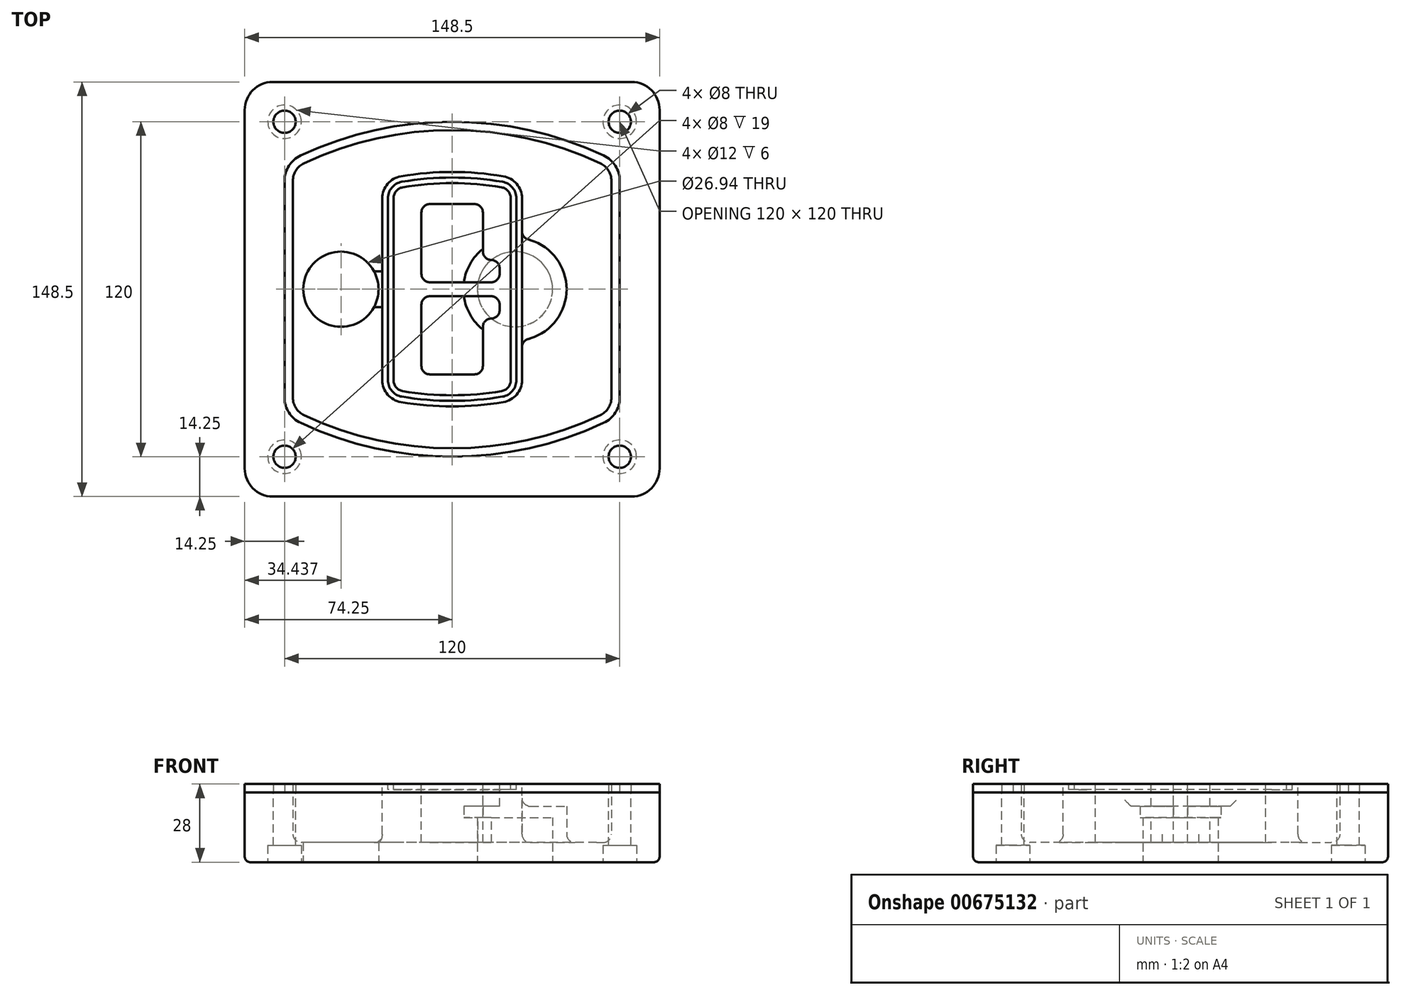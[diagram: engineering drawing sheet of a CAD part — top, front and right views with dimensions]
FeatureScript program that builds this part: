
annotation { "Feature Type Name" : "Feature", "Feature Type Description" : "" }
export const myFeature = defineFeature(function(context is Context, id is Id, definition is map)
    precondition{}
    {
        {
            var Q0;
            Q0=qCreatedBy(makeId("Top.planeOp"),FACE);
            var sketch = newSketch(context, id + "F0", { "sketchPlane" : qUnion([Q0])});
            skPoint(sketch, "E0.rect.middle", {"position": v(0, 0) * mm});
            skLineSegment(sketch, "E1.bottom", {"start": v(-64.25, -74.25) * mm, "end": v(64.25, -74.25) * mm});
            skLineSegment(sketch, "E1.top", {"start": v(-64.25, 74.25) * mm, "end": v(64.25, 74.25) * mm});
            skLineSegment(sketch, "E1.left", {"start": v(-74.25, -64.25) * mm, "end": v(-74.25, 64.25) * mm});
            skLineSegment(sketch, "E1.right", {"start": v(74.25, -64.25) * mm, "end": v(74.25, 64.25) * mm});
            skLineSegment(sketch, "E2", {"start": v(-74.25, 74.25) * mm, "end": v(74.25, -74.25) * mm, "construction": true});
            skLineSegment(sketch, "E3", {"start": v(74.25, 74.25) * mm, "end": v(-74.25, -74.25) * mm, "construction": true});
            skCircle(sketch, "E4", {"center": v(-60, 60) * mm, "radius": 4 * mm});
            skCircle(sketch, "E5", {"center": v(60, 60) * mm, "radius": 4 * mm});
            skCircle(sketch, "E6", {"center": v(60, -60) * mm, "radius": 4 * mm});
            skCircle(sketch, "E7", {"center": v(-60, -60) * mm, "radius": 4 * mm});
            skLineSegment(sketch, "E8", {"start": v(-60, 60) * mm, "end": v(60, 60) * mm, "construction": true});
            skLineSegment(sketch, "E9", {"start": v(60, 60) * mm, "end": v(60, -60) * mm, "construction": true});
            skLineSegment(sketch, "E10", {"start": v(60, -60) * mm, "end": v(-60, -60) * mm, "construction": true});
            skLineSegment(sketch, "E11", {"start": v(-60, -60) * mm, "end": v(-60, 60) * mm, "construction": true});
            skLineSegment(sketch, "E12", {"start": v(-60, 38.83) * mm, "end": v(-60, -38.83) * mm});
            skLineSegment(sketch, "E13", {"start": v(60, 38.83) * mm, "end": v(60, -38.83) * mm});
            skArc(sketch, "E14", {"start": v(54.26, 47.88) * mm, "mid": v(0, 60) * mm, "end": v(-54.26, 47.88) * mm});
            skArc(sketch, "E15", {"start": v(-54.26, -47.88) * mm, "mid": v(0, -60) * mm, "end": v(54.26, -47.88) * mm});
            skLineSegment(sketch, "E16", {"start": v(-60, 0) * mm, "end": v(60, 0) * mm, "construction": true});
            skPoint(sketch, "E17.visualSharp", {"position": v(-60, -45) * mm});
            skArc(sketch, "E17.filletArc", {"start": v(-60, -38.83) * mm, "mid": v(-58.44, -44.2) * mm, "end": v(-54.26, -47.88) * mm});
            skPoint(sketch, "E18.visualSharp", {"position": v(-60, 45) * mm});
            skArc(sketch, "E18.filletArc", {"start": v(-54.26, 47.88) * mm, "mid": v(-58.44, 44.2) * mm, "end": v(-60, 38.83) * mm});
            skPoint(sketch, "E19.visualSharp", {"position": v(60, 45) * mm});
            skArc(sketch, "E19.filletArc", {"start": v(60, 38.83) * mm, "mid": v(58.44, 44.2) * mm, "end": v(54.26, 47.88) * mm});
            skPoint(sketch, "E20.visualSharp", {"position": v(60, -45) * mm});
            skArc(sketch, "E20.filletArc", {"start": v(54.26, -47.88) * mm, "mid": v(58.44, -44.2) * mm, "end": v(60, -38.83) * mm});
            skPoint(sketch, "E21.visualSharp", {"position": v(-74.25, 74.25) * mm});
            skArc(sketch, "E21.filletArc", {"start": v(-64.25, 74.25) * mm, "mid": v(-71.32, 71.32) * mm, "end": v(-74.25, 64.25) * mm});
            skPoint(sketch, "E22.visualSharp", {"position": v(74.25, 74.25) * mm});
            skArc(sketch, "E22.filletArc", {"start": v(74.25, 64.25) * mm, "mid": v(71.32, 71.32) * mm, "end": v(64.25, 74.25) * mm});
            skPoint(sketch, "E23.visualSharp", {"position": v(74.25, -74.25) * mm});
            skArc(sketch, "E23.filletArc", {"start": v(64.25, -74.25) * mm, "mid": v(71.32, -71.32) * mm, "end": v(74.25, -64.25) * mm});
            skPoint(sketch, "E24.visualSharp", {"position": v(-74.25, -74.25) * mm});
            skArc(sketch, "E24.filletArc", {"start": v(-74.25, -64.25) * mm, "mid": v(-71.32, -71.32) * mm, "end": v(-64.25, -74.25) * mm});
            skArc(sketch, "E25.0", {"start": v(57, 38.83) * mm, "mid": v(55.9, 42.58) * mm, "end": v(52.98, 45.17) * mm});
            skLineSegment(sketch, "E25.1", {"start": v(57, 38.83) * mm, "end": v(57, -38.83) * mm});
            skArc(sketch, "E25.2", {"start": v(52.98, -45.17) * mm, "mid": v(55.9, -42.58) * mm, "end": v(57, -38.83) * mm});
            skArc(sketch, "E25.3", {"start": v(-52.98, -45.17) * mm, "mid": v(0, -57) * mm, "end": v(52.98, -45.17) * mm});
            skArc(sketch, "E25.4", {"start": v(-57, -38.83) * mm, "mid": v(-55.9, -42.58) * mm, "end": v(-52.98, -45.17) * mm});
            skArc(sketch, "E25.5", {"start": v(52.98, 45.17) * mm, "mid": v(0, 57) * mm, "end": v(-52.98, 45.17) * mm});
            skLineSegment(sketch, "E25.6", {"start": v(-57, 38.83) * mm, "end": v(-57, -38.83) * mm});
            skArc(sketch, "E25.7", {"start": v(-52.98, 45.17) * mm, "mid": v(-55.9, 42.58) * mm, "end": v(-57, 38.83) * mm});
            skArc(sketch, "E26.0", {"start": v(-55.96, 51.5) * mm, "mid": v(-61.82, 46.33) * mm, "end": v(-64, 38.83) * mm});
            skArc(sketch, "E26.1", {"start": v(55.96, 51.5) * mm, "mid": v(0, 64) * mm, "end": v(-55.96, 51.5) * mm});
            skArc(sketch, "E26.2", {"start": v(64, 38.83) * mm, "mid": v(61.82, 46.33) * mm, "end": v(55.96, 51.5) * mm});
            skLineSegment(sketch, "E26.3", {"start": v(64, 38.83) * mm, "end": v(64, -38.83) * mm});
            skArc(sketch, "E26.4", {"start": v(55.96, -51.5) * mm, "mid": v(61.82, -46.33) * mm, "end": v(64, -38.83) * mm});
            skLineSegment(sketch, "E26.5", {"start": v(-64, 38.83) * mm, "end": v(-64, -38.83) * mm});
            skArc(sketch, "E26.6", {"start": v(-55.96, -51.5) * mm, "mid": v(0, -64) * mm, "end": v(55.96, -51.5) * mm});
            skArc(sketch, "E26.7", {"start": v(-64, -38.83) * mm, "mid": v(-61.82, -46.33) * mm, "end": v(-55.96, -51.5) * mm});
            skSolve(sketch);
        }
        {
            var Q0;
            Q0=makeQuery(id+"F0.imprint","IMPRINT",FACE,{"disambiguationData":[TD([[makeQuery(id+"F0.imprint","IMPRINT",EDGE,{"derivedFrom":sQuery(id+"F0.wireOp",EDGE,"E1.bottom")}),1.0]])]});
            var Q1;
            Q1=makeQuery(id+"F0.imprint","IMPRINT",FACE,{"disambiguationData":[TD([[makeQuery(id+"F0.imprint","IMPRINT",EDGE,{"derivedFrom":sQuery(id+"F0.wireOp",EDGE,"E12")}),1.0]])]});
            var Q2;
            Q2=makeQuery(id+"F0.imprint","IMPRINT",FACE,{"disambiguationData":[TD([[makeQuery(id+"F0.imprint","IMPRINT",EDGE,{"derivedFrom":sQuery(id+"F0.wireOp",EDGE,"E25.0")}),1.0]])]});
            var Q3;
            Q3=makeQuery(id+"F0.imprint","IMPRINT",FACE,{"disambiguationData":[TD([[makeQuery(id+"F0.imprint","IMPRINT",EDGE,{"derivedFrom":sQuery(id+"F0.wireOp",EDGE,"E12")}),-1.0]])]});
            extrude(context, id + "F1", {"entities" : qUnion([Q0, Q1, Q2, Q3]), "oppositeDirection" : true, "depth" : 25 * mm});
        }
        {
            var Q0;
            Q0=makeQuery(id+"F0.imprint","IMPRINT",FACE,{"disambiguationData":[TD([[makeQuery(id+"F0.imprint","IMPRINT",EDGE,{"derivedFrom":sQuery(id+"F0.wireOp",EDGE,"E12")}),1.0]])]});
            extrude(context, id + "F2", {"entities" : qUnion([Q0]), "operationType" : NewBodyOperationType.ADD, "depth" : 3 * mm});
        }
        {
            var Q0;
            Q0=makeQuery(id+"F0.imprint","IMPRINT",FACE,{"disambiguationData":[TD([[makeQuery(id+"F0.imprint","IMPRINT",EDGE,{"derivedFrom":sQuery(id+"F0.wireOp",EDGE,"E25.0")}),1.0]])]});
            extrude(context, id + "F3", {"entities" : qUnion([Q0]), "operationType" : NewBodyOperationType.REMOVE, "oppositeDirection" : true, "depth" : 18 * mm});
        }
        {
            var Q0;
            Q0=makeQuery(id+"F2.opExtrude","CAP_FACE",FACE,{"disambiguationData":[OSD([sQuery(id+"F0.wireOp",EDGE,"E12"),sQuery(id+"F0.wireOp",EDGE,"E13"),sQuery(id+"F0.wireOp",EDGE,"E14"),sQuery(id+"F0.wireOp",EDGE,"E15"),sQuery(id+"F0.wireOp",EDGE,"E17.filletArc"),sQuery(id+"F0.wireOp",EDGE,"E18.filletArc"),sQuery(id+"F0.wireOp",EDGE,"E19.filletArc"),sQuery(id+"F0.wireOp",EDGE,"E20.filletArc"),sQuery(id+"F0.wireOp",EDGE,"E25.0"),sQuery(id+"F0.wireOp",EDGE,"E25.1"),sQuery(id+"F0.wireOp",EDGE,"E25.2"),sQuery(id+"F0.wireOp",EDGE,"E25.3"),sQuery(id+"F0.wireOp",EDGE,"E25.4"),sQuery(id+"F0.wireOp",EDGE,"E25.5"),sQuery(id+"F0.wireOp",EDGE,"E25.6"),sQuery(id+"F0.wireOp",EDGE,"E25.7")])],"isStart":false});
            var sketch = newSketch(context, id + "F4", { "sketchPlane" : qUnion([Q0])});
            skArc(sketch, "E27.0", {"start": v(-18.34, -40.45) * mm, "mid": v(0, -42) * mm, "end": v(18.34, -40.45) * mm});
            skArc(sketch, "E28.0", {"start": v(18.34, 40.45) * mm, "mid": v(0, 42) * mm, "end": v(-18.34, 40.45) * mm});
            skLineSegment(sketch, "E29", {"start": v(-25, 32.57) * mm, "end": v(-25, -32.57) * mm});
            skLineSegment(sketch, "E30", {"start": v(25, 32.57) * mm, "end": v(25, -32.57) * mm});
            skLineSegment(sketch, "E31", {"start": v(-25, 39.1) * mm, "end": v(25, 39.1) * mm, "construction": true});
            skLineSegment(sketch, "E32", {"start": v(-25, -39.1) * mm, "end": v(25, -39.1) * mm, "construction": true});
            skPoint(sketch, "E33.visualSharp", {"position": v(-25, 39.1) * mm});
            skArc(sketch, "E33.filletArc", {"start": v(-18.34, 40.45) * mm, "mid": v(-23.11, 37.73) * mm, "end": v(-25, 32.57) * mm});
            skPoint(sketch, "E34.visualSharp", {"position": v(25, 39.1) * mm});
            skArc(sketch, "E34.filletArc", {"start": v(25, 32.57) * mm, "mid": v(23.11, 37.73) * mm, "end": v(18.34, 40.45) * mm});
            skPoint(sketch, "E35.visualSharp", {"position": v(25, -39.1) * mm});
            skArc(sketch, "E35.filletArc", {"start": v(18.34, -40.45) * mm, "mid": v(23.11, -37.73) * mm, "end": v(25, -32.57) * mm});
            skPoint(sketch, "E36.visualSharp", {"position": v(-25, -39.1) * mm});
            skArc(sketch, "E36.filletArc", {"start": v(-25, -32.57) * mm, "mid": v(-23.11, -37.73) * mm, "end": v(-18.34, -40.45) * mm});
            skArc(sketch, "E37.0", {"start": v(52.98, 45.17) * mm, "mid": v(0, 57) * mm, "end": v(-52.98, 45.17) * mm});
            skArc(sketch, "E37.1", {"start": v(-52.98, 45.17) * mm, "mid": v(-55.9, 42.58) * mm, "end": v(-57, 38.83) * mm});
            skLineSegment(sketch, "E37.2", {"start": v(-57, 38.83) * mm, "end": v(-57, -38.83) * mm});
            skArc(sketch, "E37.3", {"start": v(-57, -38.83) * mm, "mid": v(-55.9, -42.58) * mm, "end": v(-52.98, -45.17) * mm});
            skArc(sketch, "E37.4", {"start": v(-52.98, -45.17) * mm, "mid": v(0, -57) * mm, "end": v(52.98, -45.17) * mm});
            skArc(sketch, "E37.5", {"start": v(52.98, -45.17) * mm, "mid": v(55.9, -42.58) * mm, "end": v(57, -38.83) * mm});
            skLineSegment(sketch, "E37.6", {"start": v(57, 38.83) * mm, "end": v(57, -38.83) * mm});
            skArc(sketch, "E37.7", {"start": v(57, 38.83) * mm, "mid": v(55.9, 42.58) * mm, "end": v(52.98, 45.17) * mm});
            skLineSegment(sketch, "E38.0", {"start": v(23, 32.57) * mm, "end": v(23, -32.57) * mm});
            skArc(sketch, "E38.1", {"start": v(18, -38.48) * mm, "mid": v(21.58, -36.44) * mm, "end": v(23, -32.57) * mm});
            skArc(sketch, "E38.2", {"start": v(-18, -38.48) * mm, "mid": v(0, -40) * mm, "end": v(18, -38.48) * mm});
            skArc(sketch, "E38.3", {"start": v(-23, -32.57) * mm, "mid": v(-21.58, -36.44) * mm, "end": v(-18, -38.48) * mm});
            skLineSegment(sketch, "E38.4", {"start": v(-23, 32.57) * mm, "end": v(-23, -32.57) * mm});
            skArc(sketch, "E38.5", {"start": v(23, 32.57) * mm, "mid": v(21.58, 36.44) * mm, "end": v(18, 38.48) * mm});
            skArc(sketch, "E38.6", {"start": v(-18, 38.48) * mm, "mid": v(-21.58, 36.44) * mm, "end": v(-23, 32.57) * mm});
            skArc(sketch, "E38.7", {"start": v(18, 38.48) * mm, "mid": v(0, 40) * mm, "end": v(-18, 38.48) * mm});
            skArc(sketch, "E39.0", {"start": v(21, 32.57) * mm, "mid": v(20.06, 35.15) * mm, "end": v(17.67, 36.5) * mm});
            skLineSegment(sketch, "E39.1", {"start": v(21, 32.57) * mm, "end": v(21, -32.57) * mm});
            skArc(sketch, "E39.2", {"start": v(17.67, -36.5) * mm, "mid": v(20.06, -35.15) * mm, "end": v(21, -32.57) * mm});
            skArc(sketch, "E39.3", {"start": v(-17.67, -36.5) * mm, "mid": v(0, -38) * mm, "end": v(17.67, -36.5) * mm});
            skArc(sketch, "E39.4", {"start": v(-21, -32.57) * mm, "mid": v(-20.06, -35.15) * mm, "end": v(-17.67, -36.5) * mm});
            skArc(sketch, "E39.5", {"start": v(17.67, 36.5) * mm, "mid": v(0, 38) * mm, "end": v(-17.67, 36.5) * mm});
            skLineSegment(sketch, "E39.6", {"start": v(-21, 32.57) * mm, "end": v(-21, -32.57) * mm});
            skArc(sketch, "E39.7", {"start": v(-17.67, 36.5) * mm, "mid": v(-20.06, 35.15) * mm, "end": v(-21, 32.57) * mm});
            skLineSegment(sketch, "E40", {"start": v(-25, 0) * mm, "end": v(25, 0) * mm, "construction": true});
            skLineSegment(sketch, "E41", {"start": v(-11, 5.5) * mm, "end": v(-11, 27.5) * mm});
            skLineSegment(sketch, "E42", {"start": v(-8, 30.5) * mm, "end": v(8, 30.5) * mm});
            skLineSegment(sketch, "E43", {"start": v(11, 27.5) * mm, "end": v(11, 13.5) * mm});
            skLineSegment(sketch, "E44", {"start": v(14, 10.5) * mm, "end": v(14, 10.5) * mm});
            skLineSegment(sketch, "E45", {"start": v(17, 7.5) * mm, "end": v(17, 5.5) * mm});
            skLineSegment(sketch, "E46", {"start": v(14, 2.5) * mm, "end": v(-8, 2.5) * mm});
            skPoint(sketch, "E47.visualSharp", {"position": v(-11, 30.5) * mm});
            skArc(sketch, "E47.filletArc", {"start": v(-8, 30.5) * mm, "mid": v(-10.12, 29.62) * mm, "end": v(-11, 27.5) * mm});
            skPoint(sketch, "E48.visualSharp", {"position": v(11, 30.5) * mm});
            skArc(sketch, "E48.filletArc", {"start": v(11, 27.5) * mm, "mid": v(10.12, 29.62) * mm, "end": v(8, 30.5) * mm});
            skPoint(sketch, "E49.visualSharp", {"position": v(11, 10.5) * mm});
            skArc(sketch, "E49.filletArc", {"start": v(11, 13.5) * mm, "mid": v(11.88, 11.38) * mm, "end": v(14, 10.5) * mm});
            skPoint(sketch, "E50.visualSharp", {"position": v(17, 10.5) * mm});
            skArc(sketch, "E50.filletArc", {"start": v(17, 7.5) * mm, "mid": v(16.12, 9.62) * mm, "end": v(14, 10.5) * mm});
            skPoint(sketch, "E51.visualSharp", {"position": v(17, 2.5) * mm});
            skArc(sketch, "E51.filletArc", {"start": v(14, 2.5) * mm, "mid": v(16.12, 3.38) * mm, "end": v(17, 5.5) * mm});
            skPoint(sketch, "E52.visualSharp", {"position": v(-11, 2.5) * mm});
            skArc(sketch, "E52.filletArc", {"start": v(-11, 5.5) * mm, "mid": v(-10.12, 3.38) * mm, "end": v(-8, 2.5) * mm});
            skLineSegment(sketch, "E53.0.MirrorCS", {"start": v(14, -2.5) * mm, "end": v(-8, -2.5) * mm});
            skArc(sketch, "E54.0.MirrorCS", {"start": v(-11, -5.5) * mm, "mid": v(-10.12, -3.38) * mm, "end": v(-8, -2.5) * mm});
            skLineSegment(sketch, "E55.0.MirrorCS", {"start": v(-11, -5.5) * mm, "end": v(-11, -27.5) * mm});
            skArc(sketch, "E56.0.MirrorCS", {"start": v(-8, -30.5) * mm, "mid": v(-10.12, -29.62) * mm, "end": v(-11, -27.5) * mm});
            skLineSegment(sketch, "E57.0.MirrorCS", {"start": v(-8, -30.5) * mm, "end": v(8, -30.5) * mm});
            skArc(sketch, "E58.0.MirrorCS", {"start": v(11, -27.5) * mm, "mid": v(10.12, -29.62) * mm, "end": v(8, -30.5) * mm});
            skLineSegment(sketch, "E59.0.MirrorCS", {"start": v(11, -27.5) * mm, "end": v(11, -13.5) * mm});
            skArc(sketch, "E60.0.MirrorCS", {"start": v(11, -13.5) * mm, "mid": v(11.88, -11.38) * mm, "end": v(14, -10.5) * mm});
            skArc(sketch, "E61.0.MirrorCS", {"start": v(17, -7.5) * mm, "mid": v(16.12, -9.62) * mm, "end": v(14, -10.5) * mm});
            skLineSegment(sketch, "E62.0.MirrorCS", {"start": v(17, -7.5) * mm, "end": v(17, -5.5) * mm});
            skArc(sketch, "E63.0.MirrorCS", {"start": v(14, -2.5) * mm, "mid": v(16.12, -3.38) * mm, "end": v(17, -5.5) * mm});
            skSolve(sketch);
        }
        {
            var Q0;
            Q0=makeQuery(id+"F4.imprint","IMPRINT",FACE,{"disambiguationData":[TD([[makeQuery(id+"F4.imprint","IMPRINT",EDGE,{"derivedFrom":sQuery(id+"F4.wireOp",EDGE,"E27.0")}),1.0]])]});
            var Q1;
            Q1=makeQuery(id+"F4.imprint","IMPRINT",FACE,{"disambiguationData":[TD([[makeQuery(id+"F4.imprint","IMPRINT",EDGE,{"derivedFrom":sQuery(id+"F4.wireOp",EDGE,"E38.0")}),-1.0]])]});
            var Q2;
            Q2=makeQuery(id+"F4.imprint","IMPRINT",FACE,{"disambiguationData":[TD([[makeQuery(id+"F4.imprint","IMPRINT",EDGE,{"derivedFrom":sQuery(id+"F4.wireOp",EDGE,"E39.0")}),1.0]])]});
            extrude(context, id + "F5", {"entities" : qUnion([Q0, Q1, Q2]), "operationType" : NewBodyOperationType.ADD, "endBound" : BoundingType.UP_TO_NEXT, "oppositeDirection" : true, "depth" : 25 * mm});
        }
        {
            var Q0;
            Q0=makeQuery(id+"F4.imprint","IMPRINT",FACE,{"disambiguationData":[TD([[makeQuery(id+"F4.imprint","IMPRINT",EDGE,{"derivedFrom":sQuery(id+"F4.wireOp",EDGE,"E38.0")}),-1.0]])]});
            extrude(context, id + "F6", {"entities" : qUnion([Q0]), "operationType" : NewBodyOperationType.REMOVE, "oppositeDirection" : true, "depth" : 2 * mm});
        }
        {
            var Q0;
            Q0=makeQuery(id+"F1.opExtrude","CAP_FACE",FACE,{"disambiguationData":[OSD([sQuery(id+"F0.wireOp",EDGE,"E1.bottom"),sQuery(id+"F0.wireOp",EDGE,"E1.top"),sQuery(id+"F0.wireOp",EDGE,"E1.left"),sQuery(id+"F0.wireOp",EDGE,"E1.right"),sQuery(id+"F0.wireOp",EDGE,"E4"),sQuery(id+"F0.wireOp",EDGE,"E5"),sQuery(id+"F0.wireOp",EDGE,"E6"),sQuery(id+"F0.wireOp",EDGE,"E7"),sQuery(id+"F0.wireOp",EDGE,"E21.filletArc"),sQuery(id+"F0.wireOp",EDGE,"E22.filletArc"),sQuery(id+"F0.wireOp",EDGE,"E23.filletArc"),sQuery(id+"F0.wireOp",EDGE,"E24.filletArc")])],"isStart":false});
            var sketch = newSketch(context, id + "F7", { "sketchPlane" : qUnion([Q0])});
            skCircle(sketch, "E64", {"center": v(22.5, 0) * mm, "radius": 13.47 * mm});
            skCircle(sketch, "E65", {"center": v(-39.81, 0) * mm, "radius": 13.47 * mm});
            skLineSegment(sketch, "E66", {"start": v(74.25, 0) * mm, "end": v(-74.25, 0) * mm});
            skCircle(sketch, "E67", {"center": v(22.5, 0) * mm, "radius": 18.47 * mm});
            skCircle(sketch, "E68", {"center": v(60, -60) * mm, "radius": 6 * mm});
            skCircle(sketch, "E69", {"center": v(-60, -60) * mm, "radius": 6 * mm});
            skCircle(sketch, "E70", {"center": v(-60, 60) * mm, "radius": 6 * mm});
            skCircle(sketch, "E71", {"center": v(60, 60) * mm, "radius": 6 * mm});
            skSolve(sketch);
        }
        {
            var Q0;
            {var subQ1=sQuery(id+"F7.wireOp",EDGE,"E66");var subQ4=sQuery(id+"F7.wireOp",EDGE,"E64");var subQ6=makeQuery(id+"F7.imprint","INTERSECT",VERTEX,{"disambiguationData":[OD(0.0)],"derivedFrom":[subQ4,subQ1]});Q0=makeQuery(id+"F7.imprint","IMPRINT",FACE,{"disambiguationData":[TD([[makeQuery(id+"F7.imprint","IMPRINT",EDGE,{"disambiguationData":[TD([[subQ6,-1.0]])],"derivedFrom":subQ4}),-1.0]])]});}
            var Q1;
            {var subQ0=sQuery(id+"F7.wireOp",EDGE,"E66");var subQ1=sQuery(id+"F7.wireOp",EDGE,"E64");var subQ3=makeQuery(id+"F7.imprint","INTERSECT",VERTEX,{"disambiguationData":[OD(0.0)],"derivedFrom":[subQ1,subQ0]});Q1=makeQuery(id+"F7.imprint","IMPRINT",FACE,{"disambiguationData":[TD([[makeQuery(id+"F7.imprint","IMPRINT",EDGE,{"disambiguationData":[TD([[subQ3,-1.0]])],"derivedFrom":subQ1}),1.0]])]});}
            var Q2;
            {var subQ0=sQuery(id+"F7.wireOp",EDGE,"E66");var subQ1=sQuery(id+"F7.wireOp",EDGE,"E64");var subQ3=makeQuery(id+"F7.imprint","INTERSECT",VERTEX,{"disambiguationData":[OD(0.0)],"derivedFrom":[subQ1,subQ0]});Q2=makeQuery(id+"F7.imprint","IMPRINT",FACE,{"disambiguationData":[TD([[makeQuery(id+"F7.imprint","IMPRINT",EDGE,{"disambiguationData":[TD([[subQ3,1.0]])],"derivedFrom":subQ1}),1.0]])]});}
            var Q3;
            {var subQ1=sQuery(id+"F7.wireOp",EDGE,"E66");var subQ4=sQuery(id+"F7.wireOp",EDGE,"E64");var subQ6=makeQuery(id+"F7.imprint","INTERSECT",VERTEX,{"disambiguationData":[OD(0.0)],"derivedFrom":[subQ4,subQ1]});Q3=makeQuery(id+"F7.imprint","IMPRINT",FACE,{"disambiguationData":[TD([[makeQuery(id+"F7.imprint","IMPRINT",EDGE,{"disambiguationData":[TD([[subQ6,1.0]])],"derivedFrom":subQ4}),-1.0]])]});}
            extrude(context, id + "F8", {"entities" : qUnion([Q0, Q1, Q2, Q3]), "operationType" : NewBodyOperationType.ADD, "oppositeDirection" : true, "depth" : 20 * mm});
        }
        {
            var Q0;
            {var subQ0=sQuery(id+"F7.wireOp",EDGE,"E66");var subQ1=sQuery(id+"F7.wireOp",EDGE,"E64");var subQ3=makeQuery(id+"F7.imprint","INTERSECT",VERTEX,{"disambiguationData":[OD(0.0)],"derivedFrom":[subQ1,subQ0]});Q0=makeQuery(id+"F7.imprint","IMPRINT",FACE,{"disambiguationData":[TD([[makeQuery(id+"F7.imprint","IMPRINT",EDGE,{"disambiguationData":[TD([[subQ3,-1.0]])],"derivedFrom":subQ1}),1.0]])]});}
            var Q1;
            {var subQ0=sQuery(id+"F7.wireOp",EDGE,"E66");var subQ1=sQuery(id+"F7.wireOp",EDGE,"E64");var subQ3=makeQuery(id+"F7.imprint","INTERSECT",VERTEX,{"disambiguationData":[OD(0.0)],"derivedFrom":[subQ1,subQ0]});Q1=makeQuery(id+"F7.imprint","IMPRINT",FACE,{"disambiguationData":[TD([[makeQuery(id+"F7.imprint","IMPRINT",EDGE,{"disambiguationData":[TD([[subQ3,1.0]])],"derivedFrom":subQ1}),1.0]])]});}
            extrude(context, id + "F9", {"entities" : qUnion([Q0, Q1]), "operationType" : NewBodyOperationType.REMOVE, "oppositeDirection" : true, "depth" : 16 * mm});
        }
        {
            var Q0;
            {var subQ0=sQuery(id+"F7.wireOp",EDGE,"E66");var subQ1=sQuery(id+"F7.wireOp",EDGE,"E65");var subQ3=makeQuery(id+"F7.imprint","INTERSECT",VERTEX,{"disambiguationData":[OD(0.0)],"derivedFrom":[subQ1,subQ0]});Q0=makeQuery(id+"F7.imprint","IMPRINT",FACE,{"disambiguationData":[TD([[makeQuery(id+"F7.imprint","IMPRINT",EDGE,{"disambiguationData":[TD([[subQ3,-1.0]])],"derivedFrom":subQ1}),1.0]])]});}
            var Q1;
            {var subQ0=sQuery(id+"F7.wireOp",EDGE,"E66");var subQ1=sQuery(id+"F7.wireOp",EDGE,"E65");var subQ3=makeQuery(id+"F7.imprint","INTERSECT",VERTEX,{"disambiguationData":[OD(0.0)],"derivedFrom":[subQ1,subQ0]});Q1=makeQuery(id+"F7.imprint","IMPRINT",FACE,{"disambiguationData":[TD([[makeQuery(id+"F7.imprint","IMPRINT",EDGE,{"disambiguationData":[TD([[subQ3,1.0]])],"derivedFrom":subQ1}),1.0]])]});}
            extrude(context, id + "F10", {"entities" : qUnion([Q0, Q1]), "operationType" : NewBodyOperationType.REMOVE, "oppositeDirection" : true, "depth" : 25 * mm});
        }
        {
            var Q0;
            Q0=makeQuery(id+"F7.imprint","IMPRINT",FACE,{"disambiguationData":[TD([[makeQuery(id+"F7.imprint","IMPRINT",EDGE,{"derivedFrom":sQuery(id+"F7.wireOp",EDGE,"E68")}),1.0]])]});
            var Q1;
            Q1=makeQuery(id+"F7.imprint","IMPRINT",FACE,{"disambiguationData":[TD([[makeQuery(id+"F7.imprint","IMPRINT",EDGE,{"derivedFrom":makeQuery(id+"F1.opExtrude","CAP_EDGE",EDGE,{"disambiguationData":[OSD([sQuery(id+"F0.wireOp",EDGE,"E5")])],"isStart":false})}),-1.0]])]});
            var Q2;
            Q2=makeQuery(id+"F7.imprint","IMPRINT",FACE,{"disambiguationData":[TD([[makeQuery(id+"F7.imprint","IMPRINT",EDGE,{"derivedFrom":sQuery(id+"F7.wireOp",EDGE,"E69")}),1.0]])]});
            var Q3;
            Q3=makeQuery(id+"F7.imprint","IMPRINT",FACE,{"disambiguationData":[TD([[makeQuery(id+"F7.imprint","IMPRINT",EDGE,{"derivedFrom":makeQuery(id+"F1.opExtrude","CAP_EDGE",EDGE,{"disambiguationData":[OSD([sQuery(id+"F0.wireOp",EDGE,"E4")])],"isStart":false})}),-1.0]])]});
            var Q4;
            Q4=makeQuery(id+"F7.imprint","IMPRINT",FACE,{"disambiguationData":[TD([[makeQuery(id+"F7.imprint","IMPRINT",EDGE,{"derivedFrom":sQuery(id+"F7.wireOp",EDGE,"E70")}),1.0]])]});
            var Q5;
            Q5=makeQuery(id+"F7.imprint","IMPRINT",FACE,{"disambiguationData":[TD([[makeQuery(id+"F7.imprint","IMPRINT",EDGE,{"derivedFrom":makeQuery(id+"F1.opExtrude","CAP_EDGE",EDGE,{"disambiguationData":[OSD([sQuery(id+"F0.wireOp",EDGE,"E7")])],"isStart":false})}),-1.0]])]});
            var Q6;
            Q6=makeQuery(id+"F7.imprint","IMPRINT",FACE,{"disambiguationData":[TD([[makeQuery(id+"F7.imprint","IMPRINT",EDGE,{"derivedFrom":sQuery(id+"F7.wireOp",EDGE,"E71")}),1.0]])]});
            var Q7;
            Q7=makeQuery(id+"F7.imprint","IMPRINT",FACE,{"disambiguationData":[TD([[makeQuery(id+"F7.imprint","IMPRINT",EDGE,{"derivedFrom":makeQuery(id+"F1.opExtrude","CAP_EDGE",EDGE,{"disambiguationData":[OSD([sQuery(id+"F0.wireOp",EDGE,"E6")])],"isStart":false})}),-1.0]])]});
            extrude(context, id + "F11", {"entities" : qUnion([Q0, Q1, Q2, Q3, Q4, Q5, Q6, Q7]), "operationType" : NewBodyOperationType.REMOVE, "oppositeDirection" : true, "depth" : 6 * mm});
        }
        {
            var Q0;
            Q0=makeQuery(id+"F9.boolean.opBoolean","COPY",FACE,{"derivedFrom":makeQuery(id+"F9.opExtrude","CAP_FACE",FACE,{"disambiguationData":[OSD([sQuery(id+"F7.wireOp",EDGE,"E64")])],"isStart":false})});
            var sketch = newSketch(context, id + "F12", { "sketchPlane" : qUnion([Q0])});
            skArc(sketch, "E72.0", {"start": v(11, 14.45) * mm, "mid": v(6.45, 9.13) * mm, "end": v(4.2, 2.5) * mm});
            skArc(sketch, "E72.1", {"start": v(4.2, -2.5) * mm, "mid": v(6.45, -9.13) * mm, "end": v(11, -14.45) * mm});
            skLineSegment(sketch, "E73", {"start": v(4.2, -2.5) * mm, "end": v(14, -2.5) * mm});
            skLineSegment(sketch, "E74.0", {"start": v(14, 2.5) * mm, "end": v(4.2, 2.5) * mm});
            skArc(sketch, "E74.1", {"start": v(14, 2.5) * mm, "mid": v(16.12, 3.38) * mm, "end": v(17, 5.5) * mm});
            skLineSegment(sketch, "E74.2", {"start": v(17, 7.5) * mm, "end": v(17, 5.5) * mm});
            skArc(sketch, "E74.3", {"start": v(17, 7.5) * mm, "mid": v(16.12, 9.62) * mm, "end": v(14, 10.5) * mm});
            skArc(sketch, "E74.4", {"start": v(11, 13.5) * mm, "mid": v(11.88, 11.38) * mm, "end": v(14, 10.5) * mm});
            skLineSegment(sketch, "E74.5", {"start": v(11, 14.45) * mm, "end": v(11, 13.5) * mm});
            skLineSegment(sketch, "E74.7", {"start": v(14, -2.5) * mm, "end": v(4.2, -2.5) * mm});
            skArc(sketch, "E74.8", {"start": v(14, -2.5) * mm, "mid": v(16.12, -3.38) * mm, "end": v(17, -5.5) * mm});
            skLineSegment(sketch, "E74.9", {"start": v(17, -7.5) * mm, "end": v(17, -5.5) * mm});
            skArc(sketch, "E74.10", {"start": v(17, -7.5) * mm, "mid": v(16.12, -9.62) * mm, "end": v(14, -10.5) * mm});
            skArc(sketch, "E74.11", {"start": v(11, -13.5) * mm, "mid": v(11.88, -11.38) * mm, "end": v(14, -10.5) * mm});
            skLineSegment(sketch, "E74.12", {"start": v(11, -14.45) * mm, "end": v(11, -13.5) * mm});
            skPoint(sketch, "E75.orphan", {"position": v(11, -27.5) * mm});
            skPoint(sketch, "E76.orphan", {"position": v(-8, -2.5) * mm});
            skPoint(sketch, "E77.orphan", {"position": v(-8, 2.5) * mm});
            skPoint(sketch, "E78.orphan", {"position": v(11, 27.5) * mm});
            skSolve(sketch);
        }
        {
            var Q0;
            {var subQ7=sQuery(id+"F12.wireOp",EDGE,"E72.0");var subQ14=sQuery(id+"F12.wireOp",EDGE,"E72.1");var subQ16=sQuery(id+"F12.wireOp",EDGE,"E74.1");var subQ18=sQuery(id+"F12.wireOp",EDGE,"E74.8");Q0=qUnion([makeQuery(id+"F12.imprint","IMPRINT",FACE,{"disambiguationData":[TD([[makeQuery(id+"F12.imprint","IMPRINT",EDGE,{"derivedFrom":subQ7}),1.0]])]}),makeQuery(id+"F12.imprint","IMPRINT",FACE,{"disambiguationData":[TD([[makeQuery(id+"F12.imprint","IMPRINT",EDGE,{"derivedFrom":subQ14}),1.0]])]}),makeQuery(id+"F12.imprint","IMPRINT",FACE,{"disambiguationData":[TD([[makeQuery(id+"F12.imprint","IMPRINT",EDGE,{"derivedFrom":subQ16}),1.0]])]}),makeQuery(id+"F12.imprint","IMPRINT",FACE,{"disambiguationData":[TD([[makeQuery(id+"F12.imprint","IMPRINT",EDGE,{"derivedFrom":subQ18}),-1.0]])]})]);}
            var Q1;
            Q1=makeQuery(id+"F5.boolean.opBoolean","SPLIT",FACE,{"disambiguationData":[TD([makeQuery(id+"F5.opExtrude","SWEPT_FACE",FACE,{"disambiguationData":[OSD([sQuery(id+"F4.wireOp",EDGE,"E41")])]})])],"derivedFrom":makeQuery(id+"F3.boolean.opBoolean","COPY",FACE,{"derivedFrom":makeQuery(id+"F3.opExtrude","CAP_FACE",FACE,{"disambiguationData":[OSD([sQuery(id+"F0.wireOp",EDGE,"E25.0"),sQuery(id+"F0.wireOp",EDGE,"E25.1"),sQuery(id+"F0.wireOp",EDGE,"E25.2"),sQuery(id+"F0.wireOp",EDGE,"E25.3"),sQuery(id+"F0.wireOp",EDGE,"E25.4"),sQuery(id+"F0.wireOp",EDGE,"E25.5"),sQuery(id+"F0.wireOp",EDGE,"E25.6"),sQuery(id+"F0.wireOp",EDGE,"E25.7")])],"isStart":false})})});
            extrude(context, id + "F13", {"entities" : qUnion([Q0]), "operationType" : NewBodyOperationType.REMOVE, "endBound" : BoundingType.UP_TO_SURFACE, "endBoundEntityFace" : qUnion([Q1]), "depth" : 25 * mm});
        }
        {
            var Q0;
            Q0=makeQuery(id+"F3.boolean.opBoolean","COPY",EDGE,{"derivedFrom":makeQuery(id+"F3.opExtrude","CAP_EDGE",EDGE,{"disambiguationData":[OSD([sQuery(id+"F0.wireOp",EDGE,"E25.6")])],"isStart":false})});
            var Q1;
            Q1=makeQuery(id+"F8.boolean.opBoolean","INTERSECT",EDGE,{"derivedFrom":[makeQuery(id+"F5.opExtrude","SWEPT_FACE",FACE,{"disambiguationData":[OSD([sQuery(id+"F4.wireOp",EDGE,"E30")])]}),makeQuery(id+"F8.opExtrude","CAP_FACE",FACE,{"disambiguationData":[OSD([sQuery(id+"F7.wireOp",EDGE,"E67")])],"isStart":false})]});
            var Q2;
            Q2=makeQuery(id+"F8.boolean.opBoolean","INTERSECT",EDGE,{"disambiguationData":[OD(1.0)],"derivedFrom":[makeQuery(id+"F5.opExtrude","SWEPT_FACE",FACE,{"disambiguationData":[OSD([sQuery(id+"F4.wireOp",EDGE,"E30")])]}),makeQuery(id+"F8.opExtrude","SWEPT_FACE",FACE,{"disambiguationData":[OSD([sQuery(id+"F7.wireOp",EDGE,"E67")])]})]});
            var Q3;
            {var subQ0=sQuery(id+"F4.wireOp",EDGE,"E30");Q3=makeQuery(id+"F8.boolean.opBoolean","SPLIT",EDGE,{"disambiguationData":[TD([makeQuery(id+"F5.opExtrude","SWEPT_FACE",FACE,{"disambiguationData":[OSD([sQuery(id+"F4.wireOp",EDGE,"E35.filletArc")])]})])],"derivedFrom":makeQuery(id+"F5.opExtrude","CAP_EDGE",EDGE,{"disambiguationData":[OSD([subQ0])],"isStart":false})});}
            var Q4;
            {var subQ0=sQuery(id+"F0.wireOp",EDGE,"E25.7");var subQ1=sQuery(id+"F0.wireOp",EDGE,"E25.1");var subQ2=sQuery(id+"F0.wireOp",EDGE,"E25.6");var subQ3=sQuery(id+"F0.wireOp",EDGE,"E25.5");var subQ4=sQuery(id+"F0.wireOp",EDGE,"E25.4");var subQ5=sQuery(id+"F0.wireOp",EDGE,"E25.0");var subQ6=sQuery(id+"F0.wireOp",EDGE,"E25.2");var subQ7=sQuery(id+"F0.wireOp",EDGE,"E25.3");Q4=makeQuery(id+"F8.boolean.opBoolean","INTERSECT",EDGE,{"derivedFrom":[makeQuery(id+"F5.boolean.opBoolean","SPLIT",FACE,{"disambiguationData":[TD([makeQuery(id+"F2.opExtrude","SWEPT_FACE",FACE,{"disambiguationData":[OSD([subQ5])]})])],"derivedFrom":makeQuery(id+"F3.boolean.opBoolean","COPY",FACE,{"derivedFrom":makeQuery(id+"F3.opExtrude","CAP_FACE",FACE,{"disambiguationData":[OSD([subQ5,subQ1,subQ6,subQ7,subQ4,subQ3,subQ2,subQ0])],"isStart":false})})}),makeQuery(id+"F8.opExtrude","SWEPT_FACE",FACE,{"disambiguationData":[OSD([sQuery(id+"F7.wireOp",EDGE,"E67")])]})]});}
            var Q5;
            Q5=makeQuery(id+"F8.boolean.opBoolean","INTERSECT",EDGE,{"disambiguationData":[OD(0.0)],"derivedFrom":[makeQuery(id+"F5.opExtrude","SWEPT_FACE",FACE,{"disambiguationData":[OSD([sQuery(id+"F4.wireOp",EDGE,"E30")])]}),makeQuery(id+"F8.opExtrude","SWEPT_FACE",FACE,{"disambiguationData":[OSD([sQuery(id+"F7.wireOp",EDGE,"E67")])]})]});
            fillet(context, id + "F14", {"entities" : qUnion([Q0, Q1, Q2, Q3, Q4, Q5]), "radius" : 3 * mm, "tangentPropagation" : true, "allowEdgeOverflow" : false});
        }
        {
            var Q0;
            Q0=makeQuery(id+"F1.opExtrude","CAP_EDGE",EDGE,{"disambiguationData":[OSD([sQuery(id+"F0.wireOp",EDGE,"E1.bottom")])],"isStart":false});
            fillet(context, id + "F15", {"entities" : qUnion([Q0]), "radius" : 2 * mm, "tangentPropagation" : true, "allowEdgeOverflow" : false});
        }
        {
            var Q0;
            {var subQ0=sQuery(id+"F0.wireOp",EDGE,"E21.filletArc");var subQ1=sQuery(id+"F0.wireOp",EDGE,"E7");var subQ2=sQuery(id+"F0.wireOp",EDGE,"E6");var subQ3=sQuery(id+"F0.wireOp",EDGE,"E5");var subQ4=sQuery(id+"F0.wireOp",EDGE,"E4");var subQ5=sQuery(id+"F0.wireOp",EDGE,"E22.filletArc");var subQ6=sQuery(id+"F0.wireOp",EDGE,"E1.bottom");var subQ7=sQuery(id+"F0.wireOp",EDGE,"E1.right");var subQ8=sQuery(id+"F0.wireOp",EDGE,"E1.top");var subQ9=sQuery(id+"F0.wireOp",EDGE,"E1.left");var subQ10=sQuery(id+"F0.wireOp",EDGE,"E23.filletArc");var subQ11=sQuery(id+"F0.wireOp",EDGE,"E24.filletArc");Q0=makeQuery(id+"F2.boolean.opBoolean","SPLIT",FACE,{"disambiguationData":[TD([makeQuery(id+"F1.opExtrude","SWEPT_FACE",FACE,{"disambiguationData":[OSD([subQ6])]})])],"derivedFrom":makeQuery(id+"F1.opExtrude","CAP_FACE",FACE,{"disambiguationData":[OSD([subQ6,subQ8,subQ9,subQ7,subQ4,subQ3,subQ2,subQ1,subQ0,subQ5,subQ10,subQ11])],"isStart":true})});}
            var sketch = newSketch(context, id + "F16", { "sketchPlane" : qUnion([Q0])});
            skArc(sketch, "E79", {"start": v(14.48, 104.25) * mm, "mid": v(0.1, 123.54) * mm, "end": v(-14.27, 104.25) * mm});
            skCircle(sketch, "E80", {"center": v(0.1, 108.54) * mm, "radius": 6 * mm});
            skLineSegment(sketch, "E81", {"start": v(0.1, 108.54) * mm, "end": v(0.1, 74.25) * mm, "construction": true});
            skPoint(sketch, "E81.endSnap0", {"position": v(0, 74.25) * mm});
            skLineSegment(sketch, "E82", {"start": v(-74.25, 0) * mm, "end": v(74.25, 0) * mm, "construction": true});
            skLineSegment(sketch, "E83", {"start": v(74.25, 0) * mm, "end": v(49.3, 0) * mm});
            skCircle(sketch, "E84.MirrorC", {"center": v(0.1, -108.54) * mm, "radius": 6 * mm});
            skPoint(sketch, "E85.MirrorP", {"position": v(0, -74.25) * mm});
            skLineSegment(sketch, "E86.MirrorCS", {"start": v(0.1, -108.54) * mm, "end": v(0.1, -74.25) * mm, "construction": true});
            skArc(sketch, "E87.MirrorCS", {"start": v(14.48, -104.25) * mm, "mid": v(0.1, -123.54) * mm, "end": v(-14.27, -104.25) * mm});
            skSolve(sketch);
        }
        {
            var Q0;
            Q0=makeQuery(id+"F16.imprint","IMPRINT",FACE,{"disambiguationData":[TD([[makeQuery(id+"F16.imprint","IMPRINT",EDGE,{"derivedFrom":makeQuery(id+"F1.opExtrude","CAP_EDGE",EDGE,{"disambiguationData":[OSD([sQuery(id+"F0.wireOp",EDGE,"E1.left")])],"isStart":true})}),-1.0]])]});
            var Q1;
            {var subQ1=sQuery(id+"F16.wireOp",EDGE,"PyDgkka8-W7HF-Lv02-yeTI-BwLbN2sV7kMK");Q1=makeQuery(id+"F16.imprint","IMPRINT",FACE,{"disambiguationData":[TD([[makeQuery(id+"F16.imprint","IMPRINT",EDGE,{"derivedFrom":subQ1}),-1.0]])]});}
            var Q2;
            Q2=makeQuery(id+"F16.imprint","IMPRINT",FACE,{"disambiguationData":[TD([[makeQuery(id+"F16.imprint","IMPRINT",EDGE,{"derivedFrom":sQuery(id+"F16.wireOp",EDGE,"1e77086e-e851-41eb-9e05-4bbe11eca9220.MirrorCS")}),1.0]])]});
            var Q3;
            {var subQ0=sQuery(id+"F4.wireOp",EDGE,"E36.filletArc");var subQ1=sQuery(id+"F4.wireOp",EDGE,"E35.filletArc");var subQ2=sQuery(id+"F4.wireOp",EDGE,"E34.filletArc");var subQ3=sQuery(id+"F4.wireOp",EDGE,"E33.filletArc");var subQ4=sQuery(id+"F4.wireOp",EDGE,"E27.0");var subQ5=sQuery(id+"F4.wireOp",EDGE,"E30");var subQ6=sQuery(id+"F4.wireOp",EDGE,"E28.0");var subQ7=sQuery(id+"F4.wireOp",EDGE,"E29");Q3=makeQuery(id+"F6.boolean.opBoolean","SPLIT",FACE,{"disambiguationData":[TD([makeQuery(id+"F5.opExtrude","SWEPT_FACE",FACE,{"disambiguationData":[OSD([subQ4])]})])],"derivedFrom":makeQuery(id+"F5.opExtrude","CAP_FACE",FACE,{"disambiguationData":[OSD([subQ4,subQ6,subQ7,subQ5,subQ3,subQ2,subQ1,subQ0,sQuery(id+"F4.wireOp",EDGE,"E41"),sQuery(id+"F4.wireOp",EDGE,"E42"),sQuery(id+"F4.wireOp",EDGE,"E43"),sQuery(id+"F4.wireOp",EDGE,"E45"),sQuery(id+"F4.wireOp",EDGE,"E46"),sQuery(id+"F4.wireOp",EDGE,"E47.filletArc"),sQuery(id+"F4.wireOp",EDGE,"E48.filletArc"),sQuery(id+"F4.wireOp",EDGE,"E49.filletArc"),sQuery(id+"F4.wireOp",EDGE,"E50.filletArc"),sQuery(id+"F4.wireOp",EDGE,"E51.filletArc"),sQuery(id+"F4.wireOp",EDGE,"E52.filletArc"),sQuery(id+"F4.wireOp",EDGE,"E53.0.MirrorCS"),sQuery(id+"F4.wireOp",EDGE,"E54.0.MirrorCS"),sQuery(id+"F4.wireOp",EDGE,"E55.0.MirrorCS"),sQuery(id+"F4.wireOp",EDGE,"E56.0.MirrorCS"),sQuery(id+"F4.wireOp",EDGE,"E57.0.MirrorCS"),sQuery(id+"F4.wireOp",EDGE,"E58.0.MirrorCS"),sQuery(id+"F4.wireOp",EDGE,"E59.0.MirrorCS"),sQuery(id+"F4.wireOp",EDGE,"E60.0.MirrorCS"),sQuery(id+"F4.wireOp",EDGE,"E61.0.MirrorCS"),sQuery(id+"F4.wireOp",EDGE,"E62.0.MirrorCS"),sQuery(id+"F4.wireOp",EDGE,"E63.0.MirrorCS")])],"isStart":true})});}
            extrude(context, id + "F17", {"entities" : qUnion([Q0, Q1, Q2]), "endBound" : BoundingType.UP_TO_SURFACE, "depth" : 25 * mm, "endBoundEntityFace" : qUnion([Q3]), "offsetDistance" : 25 * mm});
        }
    });
